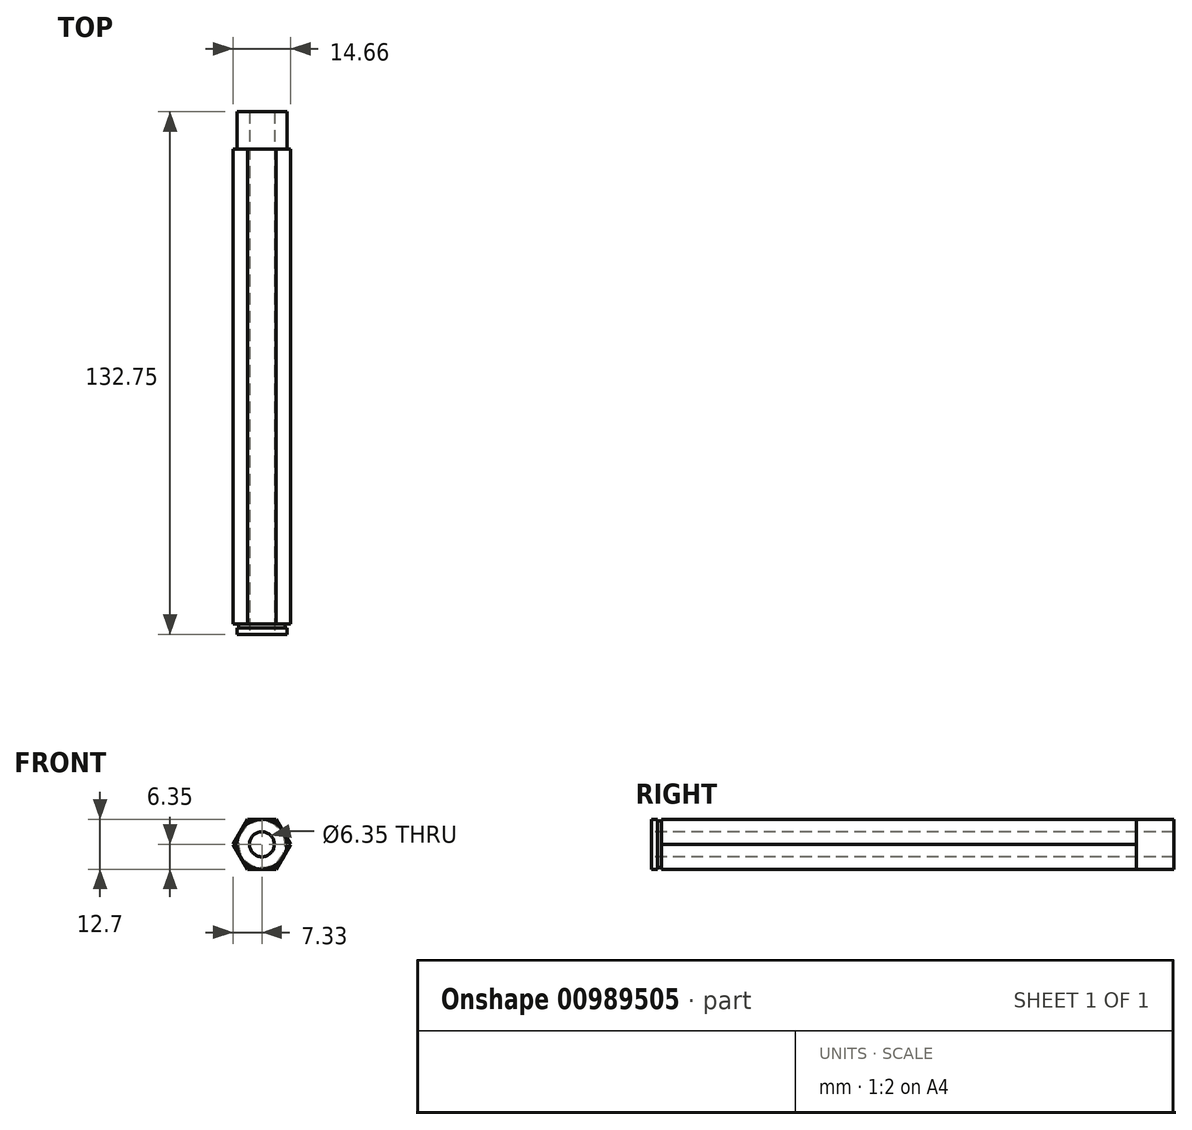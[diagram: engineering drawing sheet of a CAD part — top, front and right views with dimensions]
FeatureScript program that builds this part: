
annotation { "Feature Type Name" : "Feature", "Feature Type Description" : "" }
export const myFeature = defineFeature(function(context is Context, id is Id, definition is map)
    precondition{}
    {
        {
            var Q0;
            Q0=qCreatedBy(makeId("Front.planeOp"),FACE);
            var sketch = newSketch(context, id + "F0", { "sketchPlane" : qUnion([Q0])});
            skCircle(sketch, "E0.cCircle", {"center": v(0, 0) * mm, "radius": 6.35 * mm, "construction": true});
            skLineSegment(sketch, "E0.0", {"start": v(-3.67, 6.35) * mm, "end": v(3.67, 6.35) * mm});
            skLineSegment(sketch, "E0.1", {"start": v(3.67, 6.35) * mm, "end": v(7.33, 0) * mm});
            skLineSegment(sketch, "E0.2", {"start": v(7.33, 0) * mm, "end": v(3.67, -6.35) * mm});
            skLineSegment(sketch, "E0.3", {"start": v(3.67, -6.35) * mm, "end": v(-3.67, -6.35) * mm});
            skLineSegment(sketch, "E0.4", {"start": v(-3.67, -6.35) * mm, "end": v(-7.33, 0) * mm});
            skLineSegment(sketch, "E0.5", {"start": v(-7.33, 0) * mm, "end": v(-3.67, 6.35) * mm});
            skPoint(sketch, "E0.0.midPoint", {"position": v(0, 6.35) * mm});
            skSolve(sketch);
        }
        {
            var Q0;
            Q0=qSketchRegion(id+"F0",true);
            extrude(context, id + "F1", {"entities" : qUnion([Q0]), "depth" : 60.32 * mm, "offsetDistance" : 25.4 * mm, "hasSecondDirection" : true, "secondDirectionOppositeDirection" : true, "secondDirectionDepth" : 60.32 * mm});
        }
        {
            var Q0;
            Q0=makeQuery(id+"F1.opExtrude","CAP_FACE",FACE,{"disambiguationData":[OSD([sQuery(id+"F0.wireOp",EDGE,"E0.0"),sQuery(id+"F0.wireOp",EDGE,"E0.1"),sQuery(id+"F0.wireOp",EDGE,"E0.2"),sQuery(id+"F0.wireOp",EDGE,"E0.3"),sQuery(id+"F0.wireOp",EDGE,"E0.4"),sQuery(id+"F0.wireOp",EDGE,"E0.5")])],"isStart":false});
            var sketch = newSketch(context, id + "F2", { "sketchPlane" : qUnion([Q0])});
            skCircle(sketch, "E1", {"center": v(0, 0) * mm, "radius": 5.94 * mm});
            skSolve(sketch);
        }
        {
            var Q0;
            Q0=qSketchRegion(id+"F2",true);
            extrude(context, id + "F3", {"entities" : qUnion([Q0]), "operationType" : NewBodyOperationType.ADD, "depth" : 1 * mm, "offsetDistance" : 25.4 * mm});
        }
        {
            var Q0;
            Q0=makeQuery(id+"F3.opExtrude","CAP_FACE",FACE,{"disambiguationData":[OSD([sQuery(id+"F2.wireOp",EDGE,"E1")])],"isStart":false});
            var sketch = newSketch(context, id + "F4", { "sketchPlane" : qUnion([Q0])});
            skCircle(sketch, "E2", {"center": v(0, 0) * mm, "radius": 6.35 * mm});
            skSolve(sketch);
        }
        {
            var Q0;
            Q0=qSketchRegion(id+"F4",true);
            extrude(context, id + "F5", {"entities" : qUnion([Q0]), "operationType" : NewBodyOperationType.ADD, "depth" : 1.59 * mm, "offsetDistance" : 25.4 * mm});
        }
        {
            var Q0;
            Q0=makeQuery(id+"F5.opExtrude","CAP_FACE",FACE,{"disambiguationData":[OSD([sQuery(id+"F4.wireOp",EDGE,"E2")])],"isStart":false});
            var sketch = newSketch(context, id + "F6", { "sketchPlane" : qUnion([Q0])});
            skCircle(sketch, "E3", {"center": v(0, 0) * mm, "radius": 3.18 * mm});
            skSolve(sketch);
        }
        {
            var Q0;
            Q0 = qSketchRegion(id + "F6", true);
            extrude(context, id + "F7", {"entities" : qUnion([Q0]), "operationType" : NewBodyOperationType.REMOVE, "endBound" : BoundingType.THROUGH_ALL, "oppositeDirection" : true, "depth" : 25.4 * mm, "offsetDistance" : 25.4 * mm});
        }
        {
            var Q0;
            Q0=makeQuery(id+"F1.opExtrude","CAP_FACE",FACE,{"disambiguationData":[OSD([sQuery(id+"F0.wireOp",EDGE,"E0.0"),sQuery(id+"F0.wireOp",EDGE,"E0.1"),sQuery(id+"F0.wireOp",EDGE,"E0.2"),sQuery(id+"F0.wireOp",EDGE,"E0.3"),sQuery(id+"F0.wireOp",EDGE,"E0.4"),sQuery(id+"F0.wireOp",EDGE,"E0.5")])],"isStart":true});
            var sketch = newSketch(context, id + "F8", { "sketchPlane" : qUnion([Q0])});
            skCircle(sketch, "E4", {"center": v(0, 0) * mm, "radius": 6.35 * mm});
            skCircle(sketch, "E5", {"center": v(0, 0) * mm, "radius": 3.18 * mm});
            skSolve(sketch);
        }
        {
            var Q0;
            Q0 = qSketchRegion(id + "F8", true);
            extrude(context, id + "F9", {"entities" : qUnion([Q0]), "operationType" : NewBodyOperationType.ADD, "depth" : 9.52 * mm, "offsetDistance" : 25.4 * mm});
        }
    });
